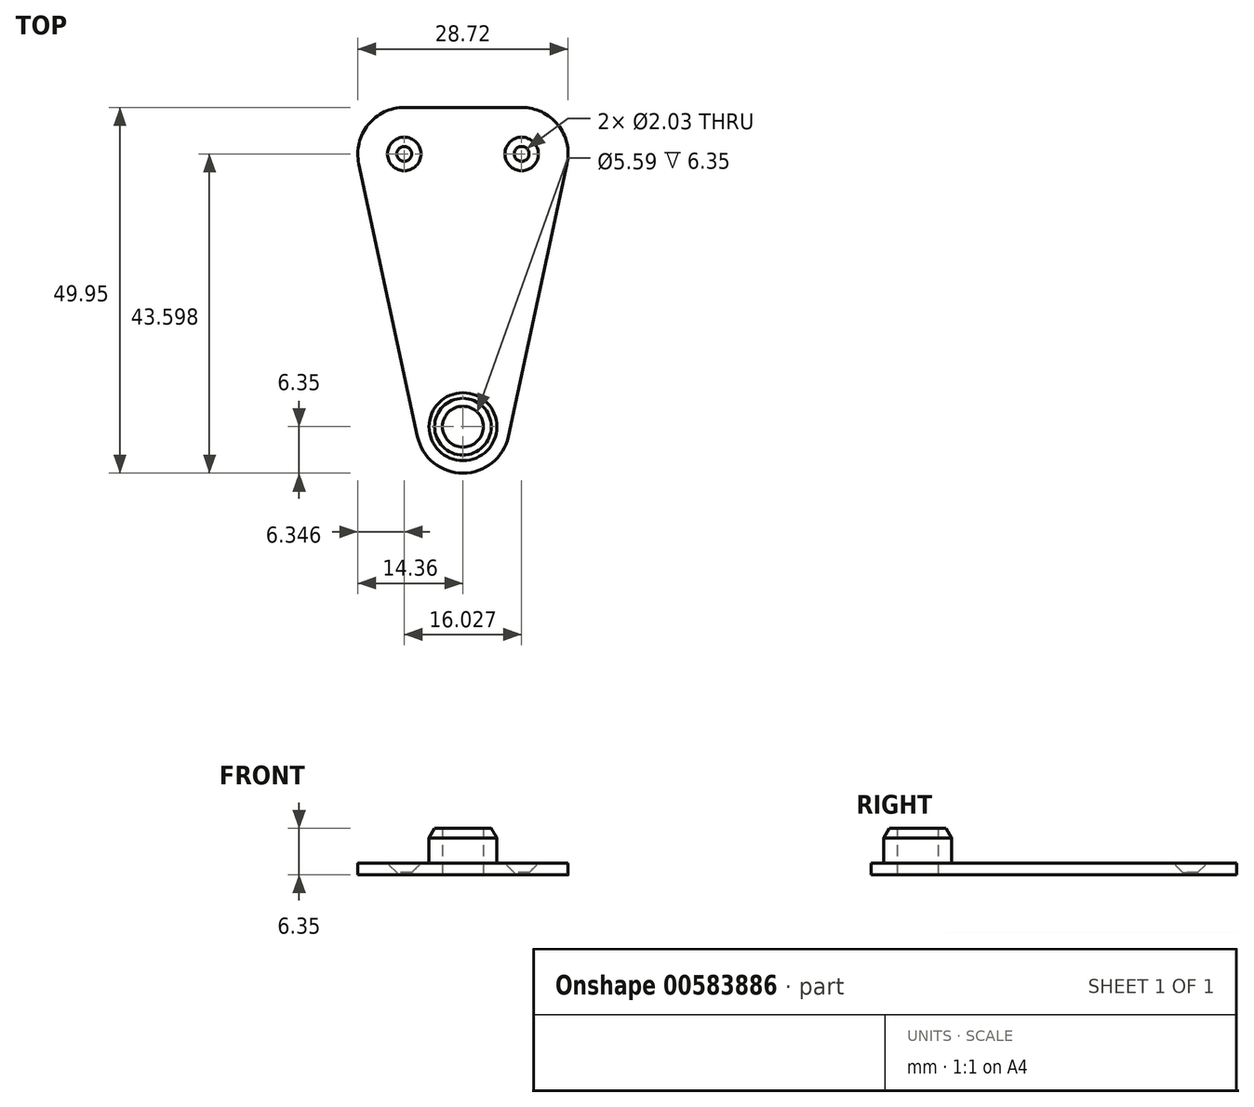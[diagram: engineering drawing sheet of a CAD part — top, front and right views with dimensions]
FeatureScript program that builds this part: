
annotation { "Feature Type Name" : "Feature", "Feature Type Description" : "" }
export const myFeature = defineFeature(function(context is Context, id is Id, definition is map)
    precondition{}
    {
        {
            var Q0;
            Q0=qCreatedBy(makeId("Top.planeOp"),FACE);
            var sketch = newSketch(context, id + "F0", { "sketchPlane" : qUnion([Q0])});
            skLineSegment(sketch, "E0", {"start": v(-6.2, -1.34) * mm, "end": v(-14.22, 35.91) * mm});
            skLineSegment(sketch, "E1", {"start": v(-8.01, 43.6) * mm, "end": v(8.01, 43.6) * mm});
            skLineSegment(sketch, "E2", {"start": v(14.22, 35.91) * mm, "end": v(6.2, -1.34) * mm});
            skCircle(sketch, "E3", {"center": v(0, 0) * mm, "radius": 4.64 * mm});
            skCircle(sketch, "E4", {"center": v(0, 0) * mm, "radius": 2.8 * mm});
            skPoint(sketch, "E5.visualSharp", {"position": v(0, -30.2) * mm});
            skArc(sketch, "E5.filletArc", {"start": v(-6.2, -1.34) * mm, "mid": v(0, -6.35) * mm, "end": v(6.2, -1.34) * mm});
            skPoint(sketch, "E6.visualSharp", {"position": v(-15.88, 43.6) * mm});
            skArc(sketch, "E6.filletArc", {"start": v(-8.01, 43.6) * mm, "mid": v(-12.95, 41.24) * mm, "end": v(-14.22, 35.91) * mm});
            skPoint(sketch, "E7.visualSharp", {"position": v(15.88, 43.6) * mm});
            skArc(sketch, "E7.filletArc", {"start": v(14.22, 35.91) * mm, "mid": v(12.95, 41.24) * mm, "end": v(8.01, 43.6) * mm});
            skCircle(sketch, "E8", {"center": v(-8.01, 37.25) * mm, "radius": 1.02 * mm});
            skCircle(sketch, "E9", {"center": v(8.01, 37.25) * mm, "radius": 1.02 * mm});
            skSolve(sketch);
        }
        {
            var Q0;
            Q0=makeQuery(id+"F0.imprint","IMPRINT",FACE,{"disambiguationData":[TD([[makeQuery(id+"F0.imprint","IMPRINT",EDGE,{"derivedFrom":sQuery(id+"F0.wireOp",EDGE,"EIfly0a4-YaIP-czMq-pG0z-FQO2pCb0yRJB")}),-1.0]])]});
            var Q1;
            Q1=makeQuery(id+"F0.imprint","IMPRINT",FACE,{"disambiguationData":[TD([[makeQuery(id+"F0.imprint","IMPRINT",EDGE,{"derivedFrom":sQuery(id+"F0.wireOp",EDGE,"E0")}),-1.0]])]});
            extrude(context, id + "F1", {"entities" : qUnion([Q0, Q1]), "depth" : 1.57 * mm, "offsetDistance" : 25.4 * mm});
        }
        {
            var Q0;
            Q0=makeQuery(id+"F0.imprint","IMPRINT",FACE,{"disambiguationData":[TD([[makeQuery(id+"F0.imprint","IMPRINT",EDGE,{"derivedFrom":sQuery(id+"F0.wireOp",EDGE,"E3")}),1.0]])]});
            extrude(context, id + "F2", {"entities" : qUnion([Q0]), "operationType" : NewBodyOperationType.ADD, "depth" : 6.35 * mm, "offsetDistance" : 25.4 * mm});
        }
        {
            var Q0;
            Q0=makeQuery(id+"F1.opExtrude","CAP_EDGE",EDGE,{"disambiguationData":[OSD([sQuery(id+"F0.wireOp",EDGE,"w7QoMWuc-IcMh-yPmd-P93v-8EEbLiyZI9uB")])],"isStart":false});
            var Q1;
            Q1=makeQuery(id+"F1.opExtrude","CAP_EDGE",EDGE,{"disambiguationData":[OSD([sQuery(id+"F0.wireOp",EDGE,"DrGieI46-XlWl-ZhtL-yxBm-75uye1BYdqBj")])],"isStart":false});
            var Q2;
            Q2=makeQuery(id+"F1.opExtrude","CAP_EDGE",EDGE,{"disambiguationData":[OSD([sQuery(id+"F0.wireOp",EDGE,"E8")])],"isStart":false});
            var Q3;
            Q3=makeQuery(id+"F1.opExtrude","CAP_EDGE",EDGE,{"disambiguationData":[OSD([sQuery(id+"F0.wireOp",EDGE,"E9")])],"isStart":false});
            chamfer(context, id + "F3", {"entities" : qUnion([Q0, Q1, Q2, Q3]), "width" : 1.27 * mm, "tangentPropagation" : true});
        }
        {
            var Q0;
            Q0=makeQuery(id+"F2.opExtrude","CAP_EDGE",EDGE,{"disambiguationData":[OSD([sQuery(id+"F0.wireOp",EDGE,"EIfly0a4-YaIP-czMq-pG0z-FQO2pCb0yRJB")])],"isStart":false});
            var Q1;
            Q1=makeQuery(id+"F2.opExtrude","CAP_EDGE",EDGE,{"disambiguationData":[OSD([sQuery(id+"F0.wireOp",EDGE,"E3")])],"isStart":false});
            chamfer(context, id + "F4", {"entities" : qUnion([Q0, Q1]), "chamferType" : ChamferType.OFFSET_ANGLE, "width" : 0.76 * mm, "oppositeDirection" : false, "angle" : 60 * degree, "tangentPropagation" : true});
        }
    });
